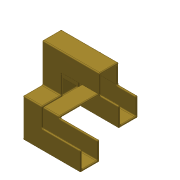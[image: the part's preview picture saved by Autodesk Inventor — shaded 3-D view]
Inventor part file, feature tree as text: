
AUTODESK INVENTOR PART (.ipt)
format: ipt  version: 2014 (Build 180170000, 170)  size: 289,280 bytes
history: native  units: in
note: dims shown in document units (in); Inventor stores cm internally (conversion verified against a paired STEP export)
features: plane x8, extrude x4, other x1, shell x1, fillet x1, sketch x1
ambient origin geometry x8: Origin, YZ Plane, XZ Plane, XY Plane, X Axis, Y Axis, Z Axis, Center Point
bodies: Solid1 (feature_tree)
feature tree (16):
  other  "Cube Master.ipt"
  extrude  "Extrusion1"  Depth=0.0193in TaperAngle=0.0deg
  extrude  "Extrusion2"  Depth=0.0193in TaperAngle=0.0deg
  extrude  "Extrusion3"  Depth=0.0193in TaperAngle=0.0deg
  extrude  "Extrusion4"  Depth=0.0193in TaperAngle=0.0deg
  shell  "Shell1"  Thickness=0.0394in
  fillet  "Fillet1"  Radius=0.0193in
  sketch  "Sketch1"  dims[d0=0.3937in d1=1.0in d2=0.0in d3=1.0in d4=0.0in d5=1.0in d6=0.0in d7=1.0in d8=0.0in d9=0.0394in d10=0.0193in d11=0.0193in]
  plane  "Work Plane1"
  plane  "Work Plane2"
  plane  "Work Plane3"
  plane  "Work Plane4"
  plane  "Work Plane5"
  plane  "Work Plane6"
  plane  "Work Plane7"
  plane  "Work Plane8"
